# Revit family: Plumbing_Valves_Bermad_710_Solenoid_Controlled_Valve Grooved 1.5in-8in
name_source: partatom
category: Pipe Accessories
units: mm (PartAtom-declared; Revit-internal decimal feet)

## family parameters
Always vertical = Yes
Cut with Voids When Loaded = No
Part Type = Valve - Breaks Into
Round Connector Dimension = Use Diameter
Shared = No
Work Plane-Based = No

## types (7) — shared parameters
700EN = No
700ES = No
700Grooved = Yes
700Threaded = No
Act_Ang = 25.00°
Assembly Code = D2020300
D_Table = 700 Revit Sizes
D_Table_Version = 2
Date of publishing = 03/10/2019
Description = Solenoid Controlled Valve
HC = No
Manufacturer = Bermad
Max Working Water Pressure = 27.6 bar
Max Working Water Temperature = 60 °C
Model = 710
PA = No
PA_8 = No
PB = No
Port_Dim = 40 mm  [stored 0.131234 ft]
Product url = www.bermad.com/product/bc-710-p/
Show Actuator Maintenance Space = No
T_from_port = 220 mm
URL = www.Bermad.com
Valve Seires = 700 Grooved

## per-type parameters (varying)
- 1.5" - DN40: Act_BD=105 mm; Ax=7 mm  [stored 0.0229659 ft]; Ay=81 mm  [stored 0.265748 ft]; Body_Dim=77 mm  [stored 0.252625 ft]; C_Plus=98 mm; D1=86 mm  [stored 0.282152 ft]; D2=125 mm; D3=85 mm  [stored 0.278871 ft]; D4=125 mm; D5=86 mm  [stored 0.282152 ft]; D6=38 mm  [stored 0.124672 ft]; Flange_Dim=48 mm  [stored 0.15748 ft]; Flange_Thick=16 mm  [stored 0.0524934 ft]; H=194 mm; H1=10 mm  [stored 0.0328084 ft]; H2=19 mm  [stored 0.062336 ft]; H3=12 mm  [stored 0.0393701 ft]; H4=32 mm  [stored 0.104987 ft]; H5=9 mm  [stored 0.0295276 ft]; K Coefficient=2.3; L=205 mm; L_Half=103 mm; Nominal Diameter=40 mm  [stored 0.131234 ft]; Port_Downx=47 mm  [stored 0.154199 ft]; Port_Upx=46 mm  [stored 0.150919 ft]; Port_W=46 mm  [stored 0.150919 ft]; Port_W2=92 mm; Port_h=40 mm  [stored 0.131234 ft]; W=122 mm; Weight=0.06 kN; h=33 mm  [stored 0.108268 ft]
- 2" - DN50: Act_BD=105 mm; Ax=7 mm  [stored 0.0229659 ft]; Ay=81 mm  [stored 0.265748 ft]; Body_Dim=77 mm  [stored 0.252625 ft]; C_Plus=98 mm; D1=86 mm  [stored 0.282152 ft]; D2=125 mm; D3=85 mm  [stored 0.278871 ft]; D4=125 mm; D5=86 mm  [stored 0.282152 ft]; D6=38 mm  [stored 0.124672 ft]; Flange_Dim=60 mm  [stored 0.19685 ft]; Flange_Thick=16 mm  [stored 0.0524934 ft]; H=201 mm; H1=10 mm  [stored 0.0328084 ft]; H2=19 mm  [stored 0.062336 ft]; H3=12 mm  [stored 0.0393701 ft]; H4=32 mm  [stored 0.104987 ft]; H5=9 mm  [stored 0.0295276 ft]; K Coefficient=3.9; L=210 mm; L_Half=105 mm; Nominal Diameter=50 mm  [stored 0.164042 ft]; Port_Downx=47 mm  [stored 0.154199 ft]; Port_Upx=46 mm  [stored 0.150919 ft]; Port_W=46 mm  [stored 0.150919 ft]; Port_W2=92 mm; Port_h=40 mm  [stored 0.131234 ft]; W=122 mm; Weight=0.06 kN; h=40 mm  [stored 0.131234 ft]
- 2.5" - DN65: Act_BD=105 mm; Ax=7 mm  [stored 0.0229659 ft]; Ay=81 mm  [stored 0.265748 ft]; Body_Dim=80 mm  [stored 0.262467 ft]; C_Plus=98 mm; D1=86 mm  [stored 0.282152 ft]; D2=125 mm; D3=85 mm  [stored 0.278871 ft]; D4=125 mm; D5=86 mm  [stored 0.282152 ft]; D6=38 mm  [stored 0.124672 ft]; Flange_Dim=76 mm; Flange_Thick=16 mm  [stored 0.0524934 ft]; H=201 mm; H1=10 mm  [stored 0.0328084 ft]; H2=19 mm  [stored 0.062336 ft]; H3=12 mm  [stored 0.0393701 ft]; H4=32 mm  [stored 0.104987 ft]; H5=9 mm  [stored 0.0295276 ft]; K Coefficient=9.2; L=215 mm; L_Half=108 mm; Nominal Diameter=65 mm  [stored 0.213255 ft]; Port_Downx=47 mm  [stored 0.154199 ft]; Port_Upx=46 mm  [stored 0.150919 ft]; Port_W=46 mm  [stored 0.150919 ft]; Port_W2=92 mm; Port_h=40 mm  [stored 0.131234 ft]; W=122 mm; Weight=0.06 kN; h=40 mm  [stored 0.131234 ft]
- 3" - DN80: Act_BD=170 mm; Ax=15 mm; Ay=117 mm; Body_Dim=85 mm  [stored 0.278871 ft]; C_Plus=144 mm; D1=104 mm; D2=153 mm; D3=110 mm; D4=165 mm; D5=124 mm; D6=42 mm  [stored 0.137795 ft]; Flange_Dim=89 mm; Flange_Thick=16 mm  [stored 0.0524934 ft]; H=265 mm; H1=16 mm  [stored 0.0524934 ft]; H2=22 mm  [stored 0.0721785 ft]; H3=22 mm  [stored 0.0721785 ft]; H4=28 mm  [stored 0.0918635 ft]; H5=23 mm  [stored 0.0754593 ft]; K Coefficient=4.9; L=250 mm; L_Half=125 mm; Nominal Diameter=80 mm  [stored 0.262467 ft]; Port_Downx=64 mm  [stored 0.209974 ft]; Port_Upx=72 mm  [stored 0.23622 ft]; Port_W=70 mm  [stored 0.229659 ft]; Port_W2=140 mm; Port_h=60 mm  [stored 0.19685 ft]; W=168 mm; Weight=0.17 kN; h=60 mm  [stored 0.19685 ft]
- 4" - DN100: Act_BD=197 mm; Ax=18 mm  [stored 0.0590551 ft]; Ay=148 mm; Body_Dim=120 mm; C_Plus=175 mm; D1=132 mm; D2=199 mm; D3=143 mm; D4=200 mm; D5=143 mm; D6=40 mm  [stored 0.131234 ft]; Flange_Dim=114 mm; Flange_Thick=16 mm  [stored 0.0524934 ft]; H=325 mm; H1=19 mm  [stored 0.062336 ft]; H2=21 mm  [stored 0.0688976 ft]; H3=26 mm; H4=31 mm  [stored 0.101706 ft]; H5=27 mm  [stored 0.0885827 ft]; K Coefficient=3.9; L=320 mm; L_Half=160 mm; Nominal Diameter=100 mm; Port_Downx=93 mm; Port_Upx=89 mm; Port_W=71 mm  [stored 0.23294 ft]; Port_W2=142 mm; Port_h=74 mm  [stored 0.242782 ft]; W=200 mm; Weight=0.28 kN; h=74 mm  [stored 0.242782 ft]
- 6" - DN150: Act_BD=252 mm; Ax=16 mm  [stored 0.0524934 ft]; Ay=197 mm; Body_Dim=172 mm; C_Plus=314 mm; D1=196 mm; D2=262 mm; D3=237 mm; D4=320 mm; D5=258 mm; D6=80 mm  [stored 0.262467 ft]; Flange_Dim=168 mm; Flange_Thick=16 mm  [stored 0.0524934 ft]; H=465 mm; H1=20 mm  [stored 0.0656168 ft]; H2=34 mm; H3=32 mm  [stored 0.104987 ft]; H4=50 mm  [stored 0.164042 ft]; H5=45 mm  [stored 0.147638 ft]; K Coefficient=3.7; L=415 mm; L_Half=208 mm; Nominal Diameter=150 mm; Port_Downx=130 mm; Port_Upx=130 mm; Port_W=102 mm; Port_W2=204 mm; Port_h=95 mm; W=320 mm; Weight=0.57 kN; h=95 mm
- 8" - DN200: Act_BD=355 mm; Ax=21 mm  [stored 0.0688976 ft]; Ay=238 mm; Body_Dim=215 mm; C_Plus=392 mm; D1=249 mm; D2=325 mm; D3=246 mm; D4=390 mm; D5=329 mm; D6=80 mm  [stored 0.262467 ft]; Flange_Dim=219 mm; Flange_Thick=19 mm  [stored 0.062336 ft]; H=529 mm; H1=20 mm  [stored 0.0656168 ft]; H2=38 mm  [stored 0.124672 ft]; H3=32 mm  [stored 0.104987 ft]; H4=60 mm  [stored 0.19685 ft]; H5=50 mm  [stored 0.164042 ft]; K Coefficient=3.8; L=500 mm; L_Half=250 mm; Nominal Diameter=200 mm; Port_Downx=170 mm; Port_Upx=170 mm; Port_W=116 mm; Port_W2=232 mm; Port_h=116 mm; W=390 mm; Weight=1.00 kN; h=125 mm

note: [stored X ft] marks values corroborated as IEEE doubles in the binary element streams (Revit-internal decimal feet)

## geometry (parser evidence)
native form markers: Sweep x5
no freeform markers — native parametric forms only
